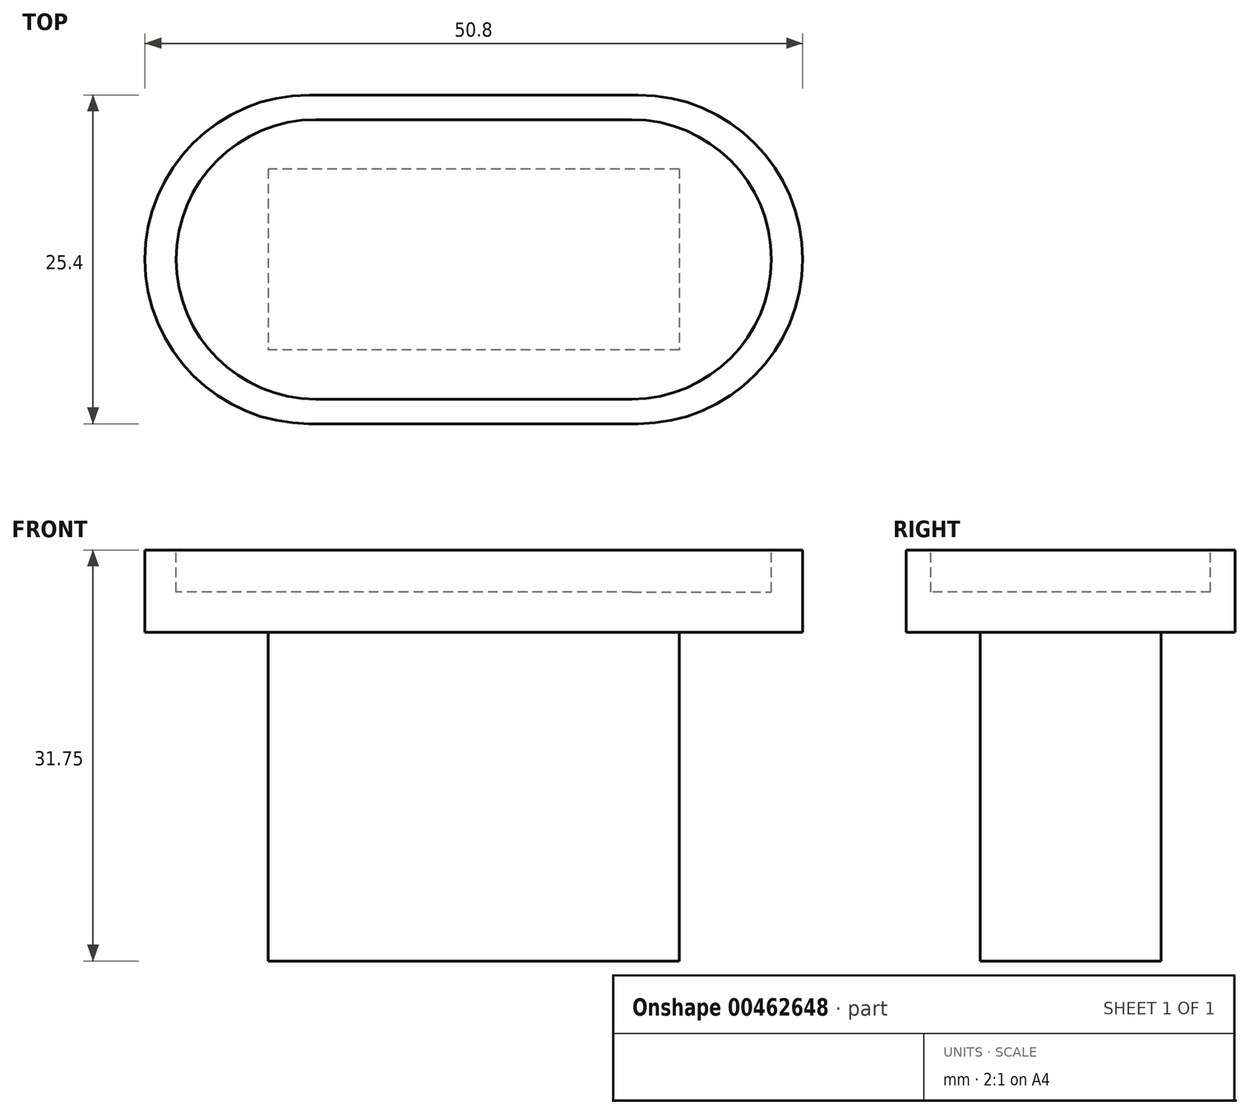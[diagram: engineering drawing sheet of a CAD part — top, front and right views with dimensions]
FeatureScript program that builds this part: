
annotation { "Feature Type Name" : "Feature", "Feature Type Description" : "" }
export const myFeature = defineFeature(function(context is Context, id is Id, definition is map)
    precondition{}
    {
        {
            var Q0;
            Q0=qCreatedBy(makeId("Top.planeOp"),FACE);
            var sketch = newSketch(context, id + "F0", { "sketchPlane" : qUnion([Q0])});
            skLineSegment(sketch, "E0", {"start": v(-88.1, 0) * mm, "end": v(98.16, 0) * mm, "construction": true});
            skLineSegment(sketch, "E1.bottom", {"start": v(12.7, -12.7) * mm, "end": v(-12.7, -12.7) * mm});
            skLineSegment(sketch, "E1.top", {"start": v(12.7, 12.7) * mm, "end": v(-12.7, 12.7) * mm});
            skPoint(sketch, "E1.middle", {"position": v(0, 0) * mm});
            skArc(sketch, "E2", {"start": v(-12.7, 12.7) * mm, "mid": v(-25.4, 0) * mm, "end": v(-12.7, -12.7) * mm});
            skArc(sketch, "E3", {"start": v(12.7, -12.7) * mm, "mid": v(25.4, 0) * mm, "end": v(12.7, 12.7) * mm});
            skSolve(sketch);
        }
        {
            var Q0;
            {var subQ0=sQuery(id+"F0.wireOp",EDGE,"E1.bottom");Q0=makeQuery(id+"F0.imprint","IMPRINT",FACE,{"disambiguationData":[TD([[makeQuery(id+"F0.imprint","IMPRINT",EDGE,{"derivedFrom":subQ0}),-1.0]])]});}
            var Q1;
            {var subQ0=sQuery(id+"F0.wireOp",EDGE,"E1.right");Q1=makeQuery(id+"F0.imprint","IMPRINT",FACE,{"disambiguationData":[TD([[makeQuery(id+"F0.imprint","IMPRINT",EDGE,{"derivedFrom":subQ0}),1.0]])]});}
            var Q2;
            {var subQ0=sQuery(id+"F0.wireOp",EDGE,"E1.left");Q2=makeQuery(id+"F0.imprint","IMPRINT",FACE,{"disambiguationData":[TD([[makeQuery(id+"F0.imprint","IMPRINT",EDGE,{"derivedFrom":subQ0}),-1.0]])]});}
            extrude(context, id + "F1", {"entities" : qUnion([Q0, Q1, Q2]), "depth" : 6.35 * mm});
        }
        {
            var Q0;
            Q0=makeQuery(id+"F1.opExtrude","CAP_FACE",FACE,{"disambiguationData":[OSD([sQuery(id+"F0.wireOp",EDGE,"E1.bottom"),sQuery(id+"F0.wireOp",EDGE,"E1.top"),sQuery(id+"F0.wireOp",EDGE,"E2"),sQuery(id+"F0.wireOp",EDGE,"E3")])],"isStart":true});
            var sketch = newSketch(context, id + "F2", { "sketchPlane" : qUnion([Q0])});
            skLineSegment(sketch, "E4.bottom", {"start": v(15.88, -6.99) * mm, "end": v(-15.88, -6.99) * mm});
            skLineSegment(sketch, "E4.top", {"start": v(15.88, 6.99) * mm, "end": v(-15.88, 6.99) * mm});
            skLineSegment(sketch, "E4.left", {"start": v(15.88, -6.99) * mm, "end": v(15.88, 6.99) * mm});
            skLineSegment(sketch, "E4.right", {"start": v(-15.88, -6.99) * mm, "end": v(-15.88, 6.99) * mm});
            skPoint(sketch, "E4.middle", {"position": v(0, 0) * mm});
            skSolve(sketch);
        }
        {
            var Q0;
            Q0 = qSketchRegion(id + "F2", true);
            extrude(context, id + "F3", {"entities" : qUnion([Q0]), "operationType" : NewBodyOperationType.ADD, "depth" : 25.4 * mm});
        }
        {
            var Q0;
            Q0=makeQuery(id+"F1.opExtrude","CAP_FACE",FACE,{"disambiguationData":[OSD([sQuery(id+"F0.wireOp",EDGE,"E1.bottom"),sQuery(id+"F0.wireOp",EDGE,"E1.top"),sQuery(id+"F0.wireOp",EDGE,"E2"),sQuery(id+"F0.wireOp",EDGE,"E3")])],"isStart":false});
            var sketch = newSketch(context, id + "F4", { "sketchPlane" : qUnion([Q0])});
            skLineSegment(sketch, "E5.bottom", {"start": v(12.2, -10.8) * mm, "end": v(-12.2, -10.8) * mm});
            skLineSegment(sketch, "E5.top", {"start": v(12.2, 10.8) * mm, "end": v(-12.2, 10.8) * mm});
            skPoint(sketch, "E5.middle", {"position": v(0, 0) * mm});
            skArc(sketch, "E6", {"start": v(-12.2, 10.8) * mm, "mid": v(-22.99, 0) * mm, "end": v(-12.2, -10.8) * mm});
            skArc(sketch, "E7", {"start": v(12.2, -10.8) * mm, "mid": v(22.99, 0) * mm, "end": v(12.2, 10.8) * mm});
            skSolve(sketch);
        }
        {
            var Q0;
            Q0=makeQuery(id+"F4.imprint","IMPRINT",FACE,{"disambiguationData":[TD([[makeQuery(id+"F4.imprint","IMPRINT",EDGE,{"derivedFrom":sQuery(id+"F4.wireOp",EDGE,"E5.bottom")}),-1.0]])]});
            extrude(context, id + "F5", {"entities" : qUnion([Q0]), "operationType" : NewBodyOperationType.REMOVE, "oppositeDirection" : true, "depth" : 3.25 * mm});
        }
    });
